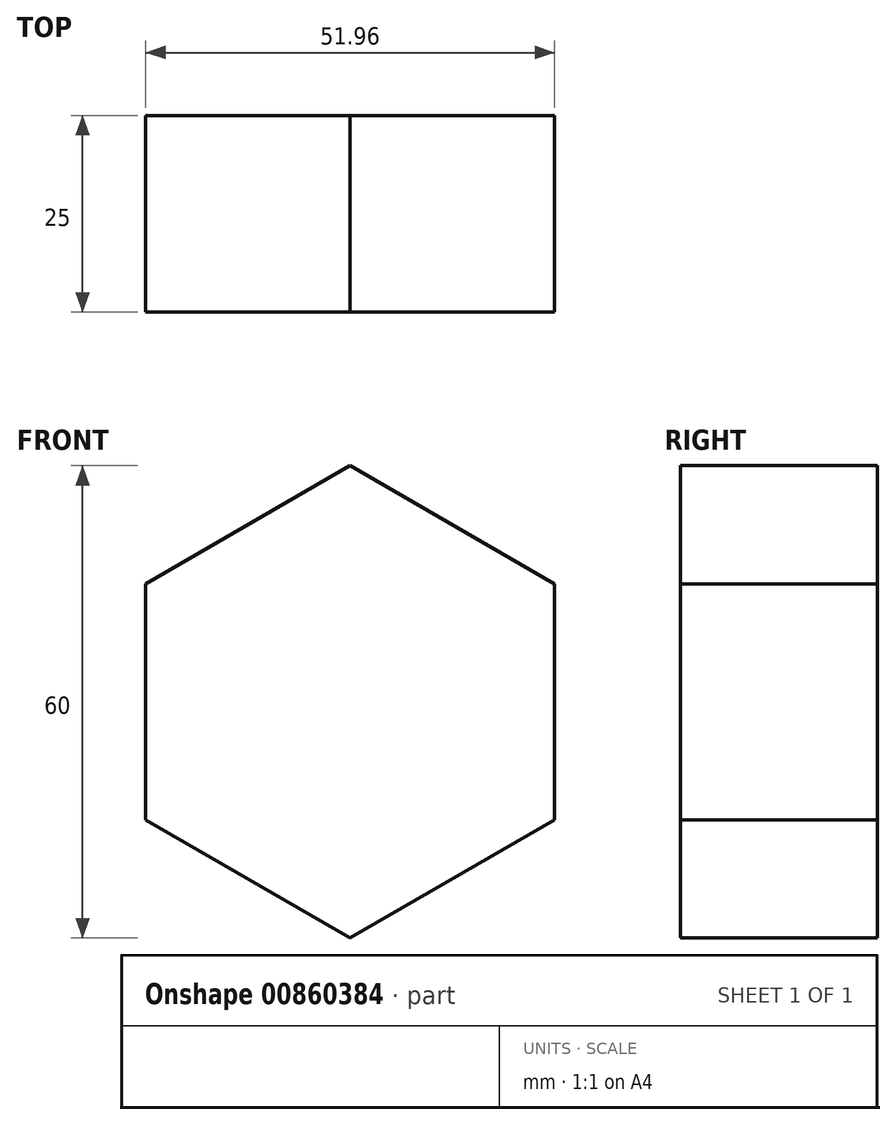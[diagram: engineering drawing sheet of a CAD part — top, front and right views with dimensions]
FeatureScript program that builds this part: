
annotation { "Feature Type Name" : "Feature", "Feature Type Description" : "" }
export const myFeature = defineFeature(function(context is Context, id is Id, definition is map)
    precondition{}
    {
        {
            var Q0;
            Q0=qCreatedBy(makeId("Front.planeOp"),FACE);
            var sketch = newSketch(context, id + "F0", { "sketchPlane" : qUnion([Q0])});
            skCircle(sketch, "E0.cCircle", {"center": v(0, 0) * mm, "radius": 25.98 * mm, "construction": true});
            skLineSegment(sketch, "E0.0", {"start": v(0, 30) * mm, "end": v(25.98, 15) * mm});
            skLineSegment(sketch, "E0.1", {"start": v(25.98, 15) * mm, "end": v(25.98, -15) * mm});
            skLineSegment(sketch, "E0.2", {"start": v(25.98, -15) * mm, "end": v(0, -30) * mm});
            skLineSegment(sketch, "E0.3", {"start": v(0, -30) * mm, "end": v(-25.98, -15) * mm});
            skLineSegment(sketch, "E0.4", {"start": v(-25.98, -15) * mm, "end": v(-25.98, 15) * mm});
            skLineSegment(sketch, "E0.5", {"start": v(-25.98, 15) * mm, "end": v(0, 30) * mm});
            skPoint(sketch, "E0.0.midPoint", {"position": v(13, 22.5) * mm});
            skSolve(sketch);
        }
        {
            var Q0;
            Q0 = qSketchRegion(id + "F0", true);
            extrude(context, id + "F1", {"entities" : qUnion([Q0]), "depth" : 25 * mm, "offsetDistance" : 25 * mm});
        }
    });
